# Revit family: 205_BSIL-50-_
name_source: partatom
category: Duct Accessories
units: mm (PartAtom-declared; Revit-internal decimal feet)

## family parameters
Always vertical = Yes
Cut with Voids When Loaded = No
Part Type = Breaks Into
Round Connector Dimension = Use Diameter
Shared = No
Work Plane-Based = No

## types (5) — shared parameters
CAT0 = Yes
Description = CIRCULAR CURVED
Manufacturer = Alnor
QmdConnectorList = 201;D;202;D
URL = http://www.ventilation-alnor.co.uk
magiPartTypeId = 205
magiProductFamilyId = BSIL-50-*

## per-type parameters (varying)
| type | CD | D | H2D | L | L2 | L2D | W2D |
| BSIL-50-125 | 224 mm  [stored 0.734908 ft] | 125 mm | 225 mm | 200 mm  [stored 0.656168 ft] | 192 mm | 200 mm  [stored 0.656168 ft] | 225 mm |
| BSIL-50-315 | 450 mm | 315 mm | 415 mm | 370 mm | 362 mm | 370 mm | 415 mm |
| BSIL-50-250 | 355 mm | 250 mm | 350 mm | 370 mm | 362 mm | 370 mm | 350 mm |
| BSIL-50-200 | 315 mm | 200 mm | 300 mm | 305 mm | 297 mm | 305 mm | 300 mm |
| BSIL-50-160 | 260 mm | 160 mm | 260 mm | 240 mm | 232 mm | 240 mm | 260 mm |

note: column(s) folded — value = type name in every type: MC Product Code, magiProductId

note: [stored X ft] marks values corroborated as IEEE doubles in the binary element streams (Revit-internal decimal feet)

## geometry (parser evidence)
native form markers: Blend x2, Sweep x3
no freeform markers — native parametric forms only
